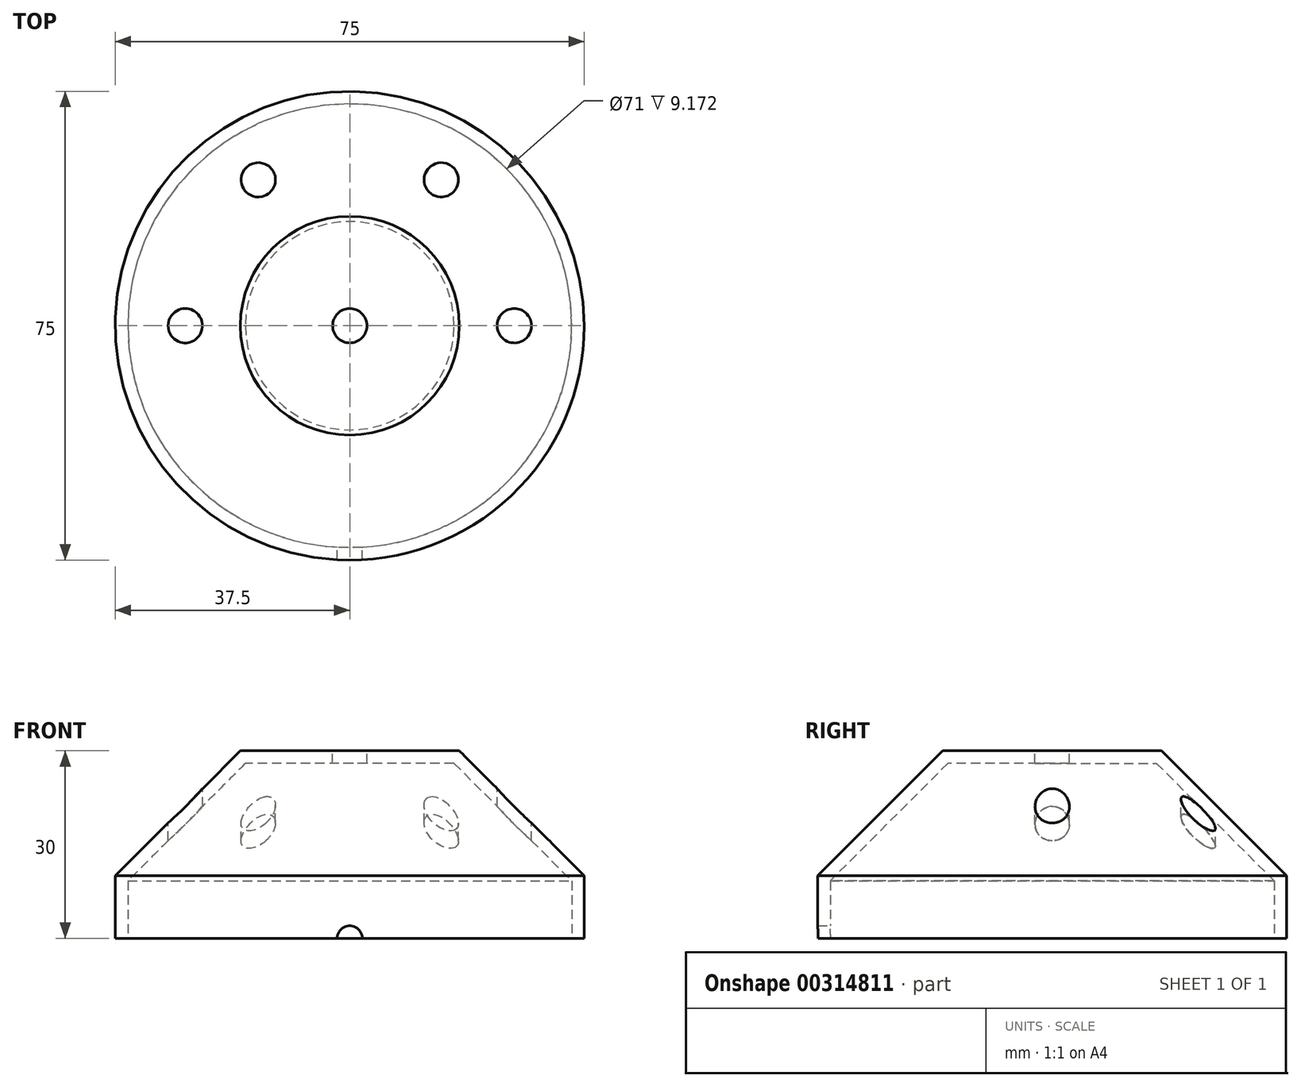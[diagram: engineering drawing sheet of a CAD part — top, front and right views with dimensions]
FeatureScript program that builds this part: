
annotation { "Feature Type Name" : "Feature", "Feature Type Description" : "" }
export const myFeature = defineFeature(function(context is Context, id is Id, definition is map)
    precondition{}
    {
        {
            var Q0;
            Q0=qCreatedBy(makeId("Top.planeOp"),FACE);
            var sketch = newSketch(context, id + "F0", { "sketchPlane" : qUnion([Q0])});
            skCircle(sketch, "E0", {"center": v(0, 0) * mm, "radius": 37.5 * mm});
            skSolve(sketch);
        }
        {
            var Q0;
            Q0 = qSketchRegion(id + "F0", true);
            extrude(context, id + "F1", {"entities" : qUnion([Q0]), "depth" : 30 * mm});
        }
        {
            var Q0;
            Q0=makeQuery(id+"F1.opExtrude","CAP_FACE",FACE,{"disambiguationData":[OSD([sQuery(id+"F0.wireOp",EDGE,"E0")])],"isStart":false});
            var sketch = newSketch(context, id + "F2", { "sketchPlane" : qUnion([Q0])});
            skCircle(sketch, "E1", {"center": v(0, 0) * mm, "radius": 2.75 * mm});
            skCircle(sketch, "E2", {"center": v(-26.31, 0) * mm, "radius": 2.75 * mm});
            skCircle(sketch, "E3", {"center": v(-14.64, 23.35) * mm, "radius": 2.75 * mm});
            skCircle(sketch, "E4.MirrorC", {"center": v(14.64, 23.35) * mm, "radius": 2.75 * mm});
            skCircle(sketch, "E5.MirrorC", {"center": v(26.31, 0) * mm, "radius": 2.75 * mm});
            skSolve(sketch);
        }
        {
            var Q0;
            Q0 = qSketchRegion(id + "F2", true);
            extrude(context, id + "F3", {"entities" : qUnion([Q0]), "operationType" : NewBodyOperationType.REMOVE, "oppositeDirection" : true, "depth" : 45 * mm});
        }
        {
            var Q0;
            Q0=makeQuery(id+"F1.opExtrude","CAP_EDGE",EDGE,{"disambiguationData":[OSD([sQuery(id+"F0.wireOp",EDGE,"E0")])],"isStart":false});
            chamfer(context, id + "F4", {"entities" : qUnion([Q0]), "width" : 20 * mm, "tangentPropagation" : true});
        }
        {
            var Q0;
            Q0=makeQuery(id+"F3.boolean.opBoolean","COPY",FACE,{"derivedFrom":makeQuery(id+"F3.opExtrude","SWEPT_FACE",FACE,{"disambiguationData":[OSD([sQuery(id+"F2.wireOp",EDGE,"E2")])]})});
            var Q1;
            Q1=makeQuery(id+"F3.boolean.opBoolean","COPY",FACE,{"derivedFrom":makeQuery(id+"F3.opExtrude","SWEPT_FACE",FACE,{"disambiguationData":[OSD([sQuery(id+"F2.wireOp",EDGE,"E1")])]})});
            var Q2;
            Q2=makeQuery(id+"F3.boolean.opBoolean","COPY",FACE,{"derivedFrom":makeQuery(id+"F3.opExtrude","SWEPT_FACE",FACE,{"disambiguationData":[OSD([sQuery(id+"F2.wireOp",EDGE,"E5.MirrorC")])]})});
            var Q3;
            Q3=makeQuery(id+"F3.boolean.opBoolean","COPY",FACE,{"derivedFrom":makeQuery(id+"F3.opExtrude","SWEPT_FACE",FACE,{"disambiguationData":[OSD([sQuery(id+"F2.wireOp",EDGE,"E4.MirrorC")])]})});
            var Q4;
            Q4=makeQuery(id+"F3.boolean.opBoolean","COPY",FACE,{"derivedFrom":makeQuery(id+"F3.opExtrude","SWEPT_FACE",FACE,{"disambiguationData":[OSD([sQuery(id+"F2.wireOp",EDGE,"E3")])]})});
            var Q5;
            Q5=makeQuery(id+"F1.opExtrude","CAP_FACE",FACE,{"disambiguationData":[OSD([sQuery(id+"F0.wireOp",EDGE,"E0")])],"isStart":true});
            shell(context, id + "F5", {"entities" : qUnion([Q0, Q1, Q2, Q3, Q4, Q5]), "thickness" : 2 * mm});
        }
        {
            var Q0;
            Q0=qCreatedBy(makeId("Front.planeOp"),FACE);
            var sketch = newSketch(context, id + "F6", { "sketchPlane" : qUnion([Q0])});
            skCircle(sketch, "E6", {"center": v(0, 0) * mm, "radius": 2 * mm});
            skSolve(sketch);
        }
        {
            var Q0;
            Q0 = qSketchRegion(id + "F6", true);
            extrude(context, id + "F7", {"entities" : qUnion([Q0]), "operationType" : NewBodyOperationType.REMOVE, "depth" : 40 * mm});
        }
    });
